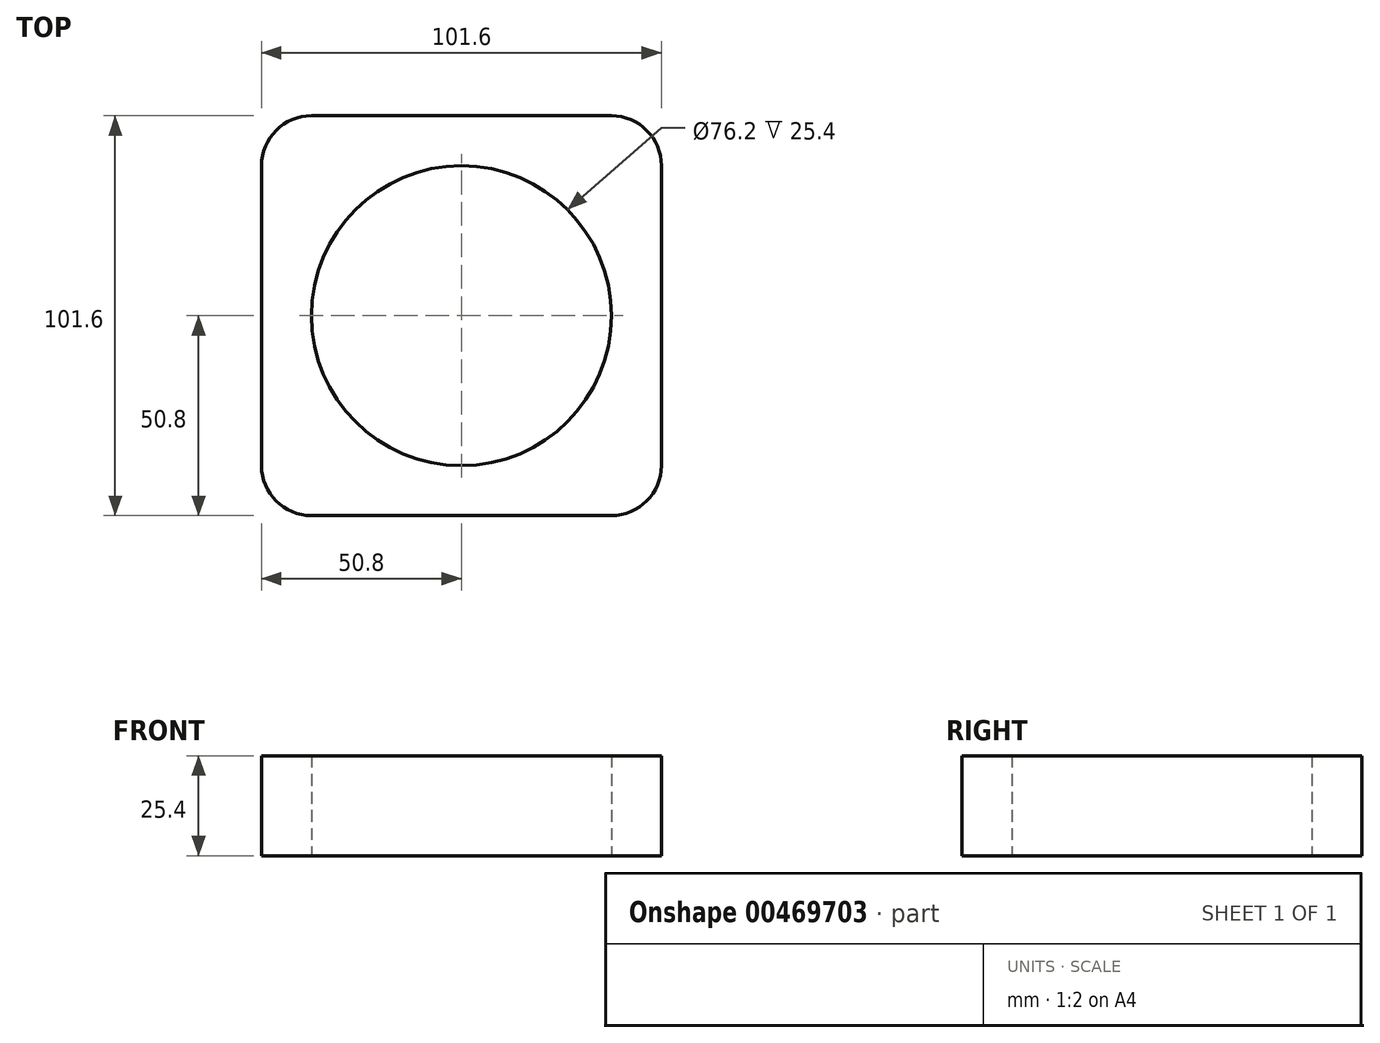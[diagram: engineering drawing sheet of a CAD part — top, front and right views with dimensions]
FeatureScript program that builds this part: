
annotation { "Feature Type Name" : "Feature", "Feature Type Description" : "" }
export const myFeature = defineFeature(function(context is Context, id is Id, definition is map)
    precondition{}
    {
        {
            var Q0;
            Q0=qCreatedBy(makeId("Top.planeOp"),FACE);
            var sketch = newSketch(context, id + "F0", { "sketchPlane" : qUnion([Q0])});
            skLineSegment(sketch, "E0.bottom", {"start": v(-38.1, 50.8) * mm, "end": v(38.1, 50.8) * mm});
            skLineSegment(sketch, "E0.top", {"start": v(-38.1, -50.8) * mm, "end": v(38.1, -50.8) * mm});
            skLineSegment(sketch, "E0.left", {"start": v(-50.8, 38.1) * mm, "end": v(-50.8, -38.1) * mm});
            skLineSegment(sketch, "E0.right", {"start": v(50.8, 38.1) * mm, "end": v(50.8, -38.1) * mm});
            skPoint(sketch, "E1.visualSharp", {"position": v(-50.8, 50.8) * mm});
            skArc(sketch, "E1.filletArc", {"start": v(-38.1, 50.8) * mm, "mid": v(-47.08, 47.08) * mm, "end": v(-50.8, 38.1) * mm});
            skPoint(sketch, "E2.visualSharp", {"position": v(50.8, 50.8) * mm});
            skArc(sketch, "E2.filletArc", {"start": v(50.8, 38.1) * mm, "mid": v(47.08, 47.08) * mm, "end": v(38.1, 50.8) * mm});
            skPoint(sketch, "E3.visualSharp", {"position": v(50.8, -50.8) * mm});
            skArc(sketch, "E3.filletArc", {"start": v(38.1, -50.8) * mm, "mid": v(47.08, -47.08) * mm, "end": v(50.8, -38.1) * mm});
            skPoint(sketch, "E4.visualSharp", {"position": v(-50.8, -50.8) * mm});
            skArc(sketch, "E4.filletArc", {"start": v(-50.8, -38.1) * mm, "mid": v(-47.08, -47.08) * mm, "end": v(-38.1, -50.8) * mm});
            skCircle(sketch, "E5", {"center": v(0, 0) * mm, "radius": 38.1 * mm});
            skSolve(sketch);
        }
        {
            var Q0;
            Q0 = qSketchRegion(id + "F0", true);
            extrude(context, id + "F1", {"entities" : qUnion([Q0]), "depth" : 25.4 * mm});
        }
    });
